# Revit family: P300122-009
name_source: partatom
category: Lighting Fixtures
revit_build: Autodesk Revit 2014 (Build: 20130308_1515(x64)
units: mm (PartAtom-declared; Revit-internal decimal feet)

## types (1)
- P300122-009
    Apparent Load = 75 VA
    Assembly Code = D5020200
    Connector Description = Lighting Connector
    Default Elevation = 48"
    Depth = 5 1/4"
    Description = Add a modern romance to the heart of your home with this lovely wall
bracket. Quiet etched glass diffusers are surrounded by clear outer shades
for a soft, luxurious touch. The shades sit on an elegant brushed nickel
frame with a rectangular backplate.
    Fixture distribution = Direct
    Glass = Hubbell - Glass
    Gold = Hubbell - Gold
    Height = 4 3/4"
    Housing Material = Paint - Hubbell - Light Silver
    Lamp = LED or incndescent
    Load Classification = Lighting
    Manufacturer = Progress Lighting
    Model = P300122-009
    Power Factor = 1
    Product Documentation Link = https://hubbellcdn.com
    Product Link = https://www.hubbell.com
    Specifications = Quiet etched glass diffusers are surrounded by clear outer shades for a
soft, luxurious touch.
• The shades sit on an elegant brushed nickel frame with a rectangular
backplate.
• Add a modern romance to the heart of your home with this lovely wall
bracket.
• Ideal for any bathroom.
• Perfect for modern, Craftsman, or contemporary settings.
• Measures 23-3/8-inch width by 7-3/8-inch height.
• Uses three medium base bulbs that are sold separately (75w max - LED,
CFL, halogen, or incandescent).
• Able to be fully dimmable with dimmable bulbs.
• Includes installation instructions and mounting hardware.
• Progress Lighting products are designed for exceptional quality, reliability,
and functionality.
    URL = https://www.hubbell.com
    Voltage = 120 V
    Warranty = 1 year Warranty
    Wattage Comments = 75W
    Watts = 75 W
    White = Paint - Hubbell - Matte White
    Width = 7 1/4"

## geometry (parser evidence)
native form markers: Sweep x5
no freeform markers — native parametric forms only
